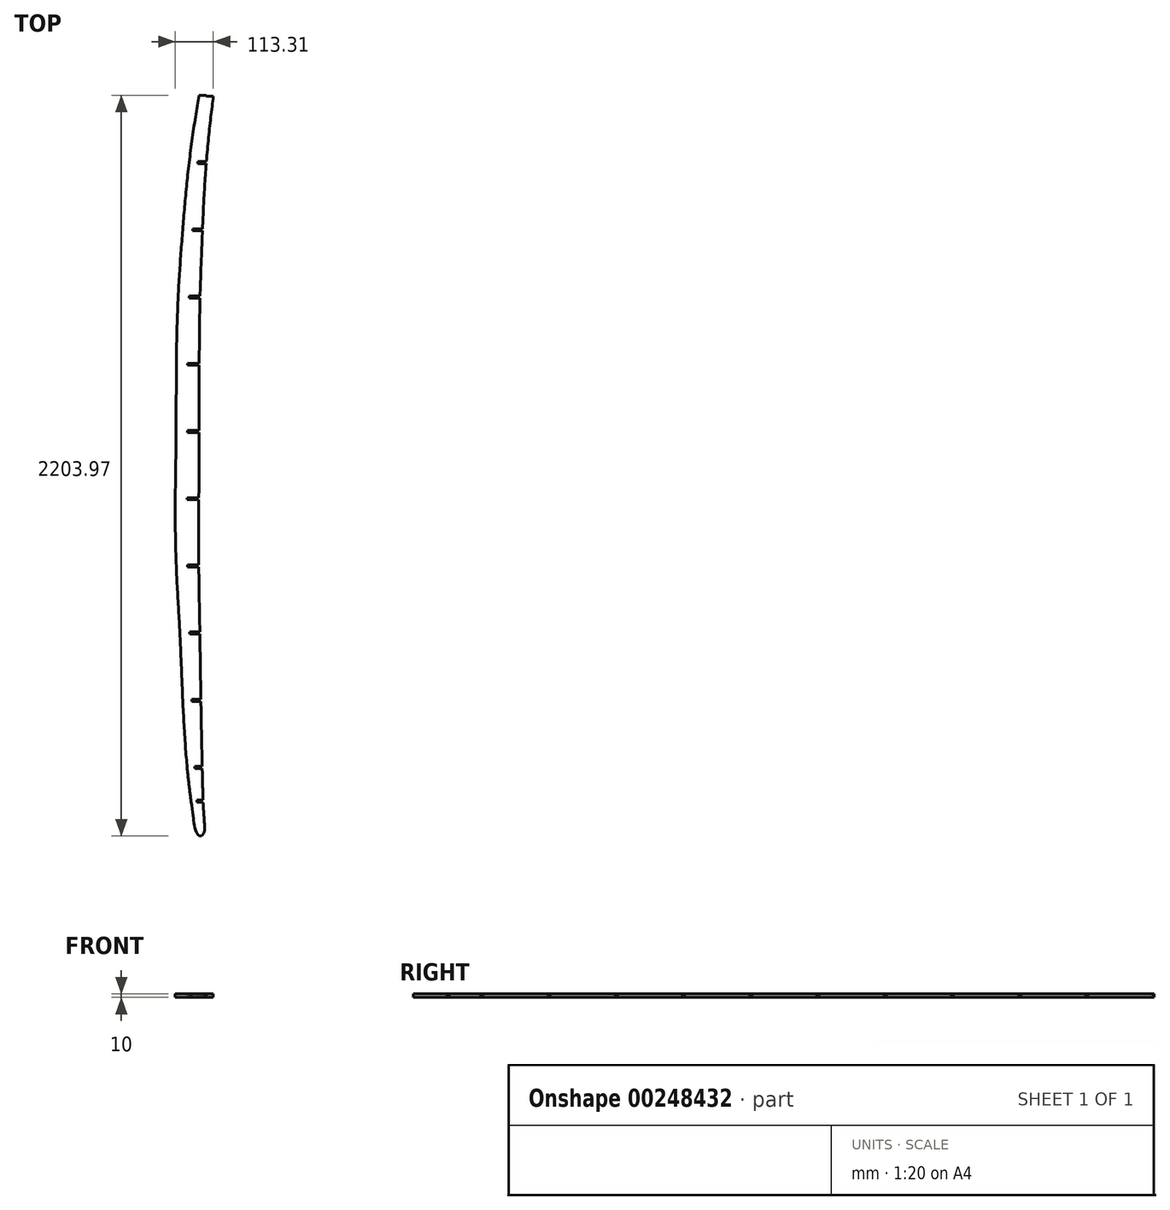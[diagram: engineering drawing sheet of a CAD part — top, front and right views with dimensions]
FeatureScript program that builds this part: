
annotation { "Feature Type Name" : "Feature", "Feature Type Description" : "" }
export const myFeature = defineFeature(function(context is Context, id is Id, definition is map)
    precondition{}
    {
        {
            var Q0;
            Q0=qCreatedBy(makeId("Top.planeOp"),FACE);
            var sketch = newSketch(context, id + "F0", { "sketchPlane" : qUnion([Q0])});
            skPoint(sketch, "E0", {"position": v(-30.92, -1091.45) * mm});
            skPoint(sketch, "E1", {"position": v(-74.7, -1091.45) * mm});
            skPoint(sketch, "E2", {"position": v(-32.04, -991.45) * mm});
            skPoint(sketch, "E3", {"position": v(-34.86, -791.45) * mm});
            skPoint(sketch, "E4", {"position": v(-87.5, -991.45) * mm});
            skPoint(sketch, "E5", {"position": v(-101.73, -791.45) * mm});
            skPoint(sketch, "E6", {"position": v(-110.44, -591.45) * mm});
            skPoint(sketch, "E7", {"position": v(-37.71, -591.45) * mm});
            skPoint(sketch, "E8", {"position": v(-40, -391.45) * mm});
            skPoint(sketch, "E9", {"position": v(-122.19, -391.45) * mm});
            skPoint(sketch, "E10", {"position": v(-125.56, -191.45) * mm});
            skPoint(sketch, "E11", {"position": v(-39.3, -191.45) * mm});
            skPoint(sketch, "E12", {"position": v(-122.68, 8.55) * mm});
            skPoint(sketch, "E13", {"position": v(-38.86, 8.55) * mm});
            skPoint(sketch, "E14", {"position": v(-38.9, 208.55) * mm});
            skPoint(sketch, "E15", {"position": v(-121.72, 208.55) * mm});
            skPoint(sketch, "E16", {"position": v(-36.32, 408.55) * mm});
            skPoint(sketch, "E17", {"position": v(-116.35, 408.55) * mm});
            skPoint(sketch, "E18", {"position": v(-29.25, 608.55) * mm});
            skPoint(sketch, "E19", {"position": v(-102.65, 608.55) * mm});
            skPoint(sketch, "E20", {"position": v(-19.1, 808.55) * mm});
            skPoint(sketch, "E21", {"position": v(-82.4, 808.55) * mm});
            skPoint(sketch, "E22", {"position": v(1.8, 1008.55) * mm});
            skPoint(sketch, "E23", {"position": v(-52.56, 1008.55) * mm});
            skPoint(sketch, "E24", {"position": v(14.1, 1108.55) * mm});
            skPoint(sketch, "E25", {"position": v(-32.64, 1108.55) * mm});
            skPoint(sketch, "E26", {"position": v(-32.6, 1108.55) * mm});
            skLineSegment(sketch, "E27", {"start": v(14.1, 1108.55) * mm, "end": v(-32.64, 1108.55) * mm});
            skLineSegment(sketch, "E28", {"start": v(1.8, 1008.55) * mm, "end": v(-52.56, 1008.55) * mm});
            skLineSegment(sketch, "E29", {"start": v(-25.38, 1008.55) * mm, "end": v(1.8, 1008.55) * mm});
            skLineSegment(sketch, "E30", {"start": v(-19.1, 808.55) * mm, "end": v(-82.4, 808.55) * mm});
            skPoint(sketch, "E31.endSnap0", {"position": v(-50.75, 808.55) * mm});
            skLineSegment(sketch, "E32", {"start": v(-29.25, 608.55) * mm, "end": v(-102.65, 608.55) * mm});
            skLineSegment(sketch, "E33", {"start": v(-36.32, 408.55) * mm, "end": v(-116.35, 408.55) * mm});
            skLineSegment(sketch, "E34", {"start": v(-38.9, 208.55) * mm, "end": v(-121.72, 208.55) * mm});
            skLineSegment(sketch, "E35", {"start": v(-38.86, 8.55) * mm, "end": v(-122.68, 8.55) * mm});
            skLineSegment(sketch, "E36", {"start": v(-39.3, -191.45) * mm, "end": v(-125.56, -191.45) * mm});
            skLineSegment(sketch, "E37", {"start": v(-40, -391.45) * mm, "end": v(-122.19, -391.45) * mm});
            skLineSegment(sketch, "E38", {"start": v(-37.71, -591.45) * mm, "end": v(-110.44, -591.45) * mm});
            skLineSegment(sketch, "E39", {"start": v(-34.86, -791.45) * mm, "end": v(-101.73, -791.45) * mm});
            skLineSegment(sketch, "E40", {"start": v(-34.86, -791.45) * mm, "end": v(-68.3, -791.45) * mm});
            skLineSegment(sketch, "E41", {"start": v(-32.04, -991.45) * mm, "end": v(-87.5, -991.45) * mm});
            skLineSegment(sketch, "E42", {"start": v(-30.92, -1091.45) * mm, "end": v(-74.7, -1091.45) * mm});
            skPoint(sketch, "E43.endSnap0", {"position": v(-52.82, -1091.45) * mm});
            skLineSegment(sketch, "E44", {"start": v(-32.64, 1108.55) * mm, "end": v(-28.25, 1108.55) * mm});
            skLineSegment(sketch, "E45", {"start": v(-28.25, 1108.55) * mm, "end": v(9.75, 1108.55) * mm});
            skLineSegment(sketch, "E46", {"start": v(9.75, 1108.55) * mm, "end": v(14.1, 1108.55) * mm});
            skLineSegment(sketch, "E47", {"start": v(14.02, 1212.5) * mm, "end": v(14.02, 1243.38) * mm});
            skLineSegment(sketch, "E48", {"start": v(27.97, 1200.3) * mm, "end": v(27.97, 1247.02) * mm});
            skFitSpline(sketch, "E49", {"points": [v(9.75, 1108.55) * mm, v(20.39, 1156.4) * mm, v(23.47, 1182.1) * mm, v(20.65, 1203.18) * mm, v(14.02, 1212.5) * mm, v(2.91, 1207.55) * mm, v(-4.03, 1195.2) * mm, v(-15.85, 1160.5) * mm, v(-28.25, 1108.55) * mm], "startDerivative": vector(69.99, 299.65) * mm, "endDerivative": vector(-63.8, -297.22) * mm});
            skLineSegment(sketch, "E50", {"start": v(-52.56, 1008.55) * mm, "end": v(-46.89, 1008.55) * mm});
            skLineSegment(sketch, "E51", {"start": v(-46.89, 1008.55) * mm, "end": v(-3.88, 1008.55) * mm});
            skLineSegment(sketch, "E52", {"start": v(-3.88, 1008.55) * mm, "end": v(1.8, 1008.55) * mm});
            skLineSegment(sketch, "E53", {"start": v(-19.1, 808.55) * mm, "end": v(-25.25, 808.55) * mm});
            skLineSegment(sketch, "E54", {"start": v(-25.25, 808.55) * mm, "end": v(-76.25, 808.55) * mm});
            skLineSegment(sketch, "E55", {"start": v(-76.25, 808.55) * mm, "end": v(-82.4, 808.55) * mm});
            skLineSegment(sketch, "E56", {"start": v(-29.25, 608.55) * mm, "end": v(-36.45, 608.55) * mm});
            skLineSegment(sketch, "E57", {"start": v(-36.45, 608.55) * mm, "end": v(-95.45, 608.55) * mm});
            skLineSegment(sketch, "E58", {"start": v(-95.45, 608.55) * mm, "end": v(-102.65, 608.55) * mm});
            skLineSegment(sketch, "E59", {"start": v(-36.32, 408.55) * mm, "end": v(-43.82, 408.55) * mm});
            skLineSegment(sketch, "E60", {"start": v(-43.82, 408.55) * mm, "end": v(-108.85, 408.55) * mm});
            skLineSegment(sketch, "E61", {"start": v(-108.85, 408.55) * mm, "end": v(-116.35, 408.55) * mm});
            skLineSegment(sketch, "E62", {"start": v(-38.9, 208.55) * mm, "end": v(-46.3, 208.55) * mm});
            skLineSegment(sketch, "E63", {"start": v(-46.3, 208.55) * mm, "end": v(-114.32, 208.55) * mm});
            skLineSegment(sketch, "E64", {"start": v(-114.32, 208.55) * mm, "end": v(-121.72, 208.55) * mm});
            skLineSegment(sketch, "E65", {"start": v(-38.86, 8.55) * mm, "end": v(-46.57, 8.55) * mm});
            skLineSegment(sketch, "E66", {"start": v(-46.57, 8.55) * mm, "end": v(-114.97, 8.55) * mm});
            skLineSegment(sketch, "E67", {"start": v(-114.97, 8.55) * mm, "end": v(-122.68, 8.55) * mm});
            skLineSegment(sketch, "E68", {"start": v(-39.3, -191.45) * mm, "end": v(-47.42, -191.45) * mm});
            skLineSegment(sketch, "E69", {"start": v(-47.42, -191.45) * mm, "end": v(-117.43, -191.45) * mm});
            skLineSegment(sketch, "E70", {"start": v(-117.43, -191.45) * mm, "end": v(-125.56, -191.45) * mm});
            skLineSegment(sketch, "E71", {"start": v(-40, -391.45) * mm, "end": v(-47.6, -391.45) * mm});
            skLineSegment(sketch, "E72", {"start": v(-47.6, -391.45) * mm, "end": v(-114.6, -391.45) * mm});
            skLineSegment(sketch, "E73", {"start": v(-114.6, -391.45) * mm, "end": v(-122.19, -391.45) * mm});
            skLineSegment(sketch, "E74", {"start": v(-37.71, -591.45) * mm, "end": v(-44.37, -591.45) * mm});
            skLineSegment(sketch, "E75", {"start": v(-44.37, -591.45) * mm, "end": v(-103.78, -591.45) * mm});
            skLineSegment(sketch, "E76", {"start": v(-103.78, -591.45) * mm, "end": v(-110.44, -591.45) * mm});
            skLineSegment(sketch, "E77", {"start": v(-34.86, -791.45) * mm, "end": v(-41.3, -791.45) * mm});
            skLineSegment(sketch, "E78", {"start": v(-41.3, -791.45) * mm, "end": v(-95.29, -791.45) * mm});
            skLineSegment(sketch, "E79", {"start": v(-95.29, -791.45) * mm, "end": v(-101.73, -791.45) * mm});
            skLineSegment(sketch, "E80", {"start": v(-32.04, -991.45) * mm, "end": v(-37.39, -991.45) * mm});
            skLineSegment(sketch, "E81", {"start": v(-37.39, -991.45) * mm, "end": v(-82.16, -991.45) * mm});
            skLineSegment(sketch, "E82", {"start": v(-82.16, -991.45) * mm, "end": v(-87.5, -991.45) * mm});
            skLineSegment(sketch, "E83", {"start": v(-30.92, -1091.45) * mm, "end": v(-35.01, -1091.45) * mm});
            skLineSegment(sketch, "E84", {"start": v(-35.01, -1091.45) * mm, "end": v(-70.62, -1091.45) * mm});
            skLineSegment(sketch, "E85", {"start": v(-70.62, -1091.45) * mm, "end": v(-74.7, -1091.45) * mm});
            skFitSpline(sketch, "E86", {"points": [v(9.75, 1108.55) * mm, v(-3.88, 1008.55) * mm, v(-25.25, 808.55) * mm, v(-36.45, 608.55) * mm, v(-43.82, 408.55) * mm, v(-46.3, 208.55) * mm, v(-46.57, 8.55) * mm, v(-47.42, -191.45) * mm, v(-47.6, -391.45) * mm, v(-44.37, -591.45) * mm, v(-41.3, -791.45) * mm, v(-37.39, -991.45) * mm, v(-35.01, -1091.45) * mm], "startDerivative": vector(-207.13, -1457.4) * mm, "endDerivative": vector(36.18, -1464.69) * mm});
            skFitSpline(sketch, "E87", {"points": [v(-35.01, -1091.45) * mm, v(-33.1, -1121.3) * mm, v(-30.99, -1153.32) * mm], "startDerivative": vector(3.84, -60.24) * mm, "endDerivative": vector(4.21, -63.47) * mm});
            skFitSpline(sketch, "E88", {"points": [v(-28.25, 1108.55) * mm, v(-46.89, 1008.55) * mm, v(-76.25, 808.55) * mm, v(-95.45, 608.55) * mm, v(-108.85, 408.55) * mm, v(-114.32, 208.55) * mm, v(-114.97, 8.55) * mm, v(-117.43, -191.45) * mm, v(-114.6, -391.45) * mm, v(-103.78, -591.45) * mm, v(-95.29, -791.45) * mm, v(-82.16, -991.45) * mm, v(-70.62, -1091.45) * mm], "startDerivative": vector(-284.6, -1452.48) * mm, "endDerivative": vector(190.25, -1460.4) * mm});
            skFitSpline(sketch, "E89", {"points": [v(-70.62, -1091.45) * mm, v(-63.97, -1136.64) * mm, v(-61.87, -1157.67) * mm, v(-56.4, -1179.96) * mm, v(-50.93, -1190.9) * mm, v(-43.78, -1195.41) * mm, v(-36.63, -1191.74) * mm, v(-31.59, -1182.06) * mm, v(-30.32, -1169.87) * mm, v(-30.99, -1153.32) * mm], "startDerivative": vector(43.58, -267.95) * mm, "endDerivative": vector(-8.77, 152.7) * mm});
            skLineSegment(sketch, "E90", {"start": v(9.75, 1108.55) * mm, "end": v(-9.25, 1108.55) * mm});
            skLineSegment(sketch, "E91", {"start": v(-9.25, 1108.55) * mm, "end": v(-9.25, 1111.55) * mm});
            skLineSegment(sketch, "E92", {"start": v(-9.25, 1108.55) * mm, "end": v(-9.25, 1105.55) * mm});
            skLineSegment(sketch, "E93", {"start": v(-9.25, 1111.55) * mm, "end": v(10.45, 1111.55) * mm});
            skLineSegment(sketch, "E94", {"start": v(-9.25, 1105.55) * mm, "end": v(9.32, 1105.55) * mm});
            skLineSegment(sketch, "E95", {"start": v(-25.38, 1008.55) * mm, "end": v(-25.38, 1011.55) * mm});
            skLineSegment(sketch, "E96", {"start": v(-25.38, 1008.55) * mm, "end": v(-25.38, 1005.55) * mm});
            skLineSegment(sketch, "E97", {"start": v(-25.38, 1011.55) * mm, "end": v(-3.5, 1011.55) * mm});
            skLineSegment(sketch, "E98", {"start": v(-25.38, 1005.55) * mm, "end": v(-4.26, 1005.55) * mm});
            skLineSegment(sketch, "E99", {"start": v(-50.75, 808.55) * mm, "end": v(-50.75, 811.55) * mm});
            skLineSegment(sketch, "E100", {"start": v(-50.75, 808.55) * mm, "end": v(-50.8, 805.55) * mm});
            skLineSegment(sketch, "E101", {"start": v(-50.75, 811.55) * mm, "end": v(-25, 811.55) * mm});
            skLineSegment(sketch, "E102", {"start": v(-50.8, 805.55) * mm, "end": v(-25.5, 805.55) * mm});
            skLineSegment(sketch, "E103", {"start": v(-65.95, 608.55) * mm, "end": v(-65.95, 611.55) * mm});
            skPoint(sketch, "E103.endSnap0", {"position": v(-65.95, 608.55) * mm});
            skLineSegment(sketch, "E104", {"start": v(-65.95, 608.55) * mm, "end": v(-65.95, 605.55) * mm});
            skLineSegment(sketch, "E105", {"start": v(-65.95, 605.55) * mm, "end": v(-36.58, 605.55) * mm});
            skLineSegment(sketch, "E106", {"start": v(-65.95, 611.55) * mm, "end": v(-36.32, 611.55) * mm});
            skLineSegment(sketch, "E107", {"start": v(-76.34, 408.55) * mm, "end": v(-76.34, 411.55) * mm});
            skLineSegment(sketch, "E108", {"start": v(-76.34, 408.55) * mm, "end": v(-76.34, 405.55) * mm});
            skLineSegment(sketch, "E109", {"start": v(-76.34, 411.55) * mm, "end": v(-43.75, 411.55) * mm});
            skLineSegment(sketch, "E110", {"start": v(-76.34, 405.55) * mm, "end": v(-43.9, 405.55) * mm});
            skLineSegment(sketch, "E111", {"start": v(-80.31, 208.55) * mm, "end": v(-80.31, 211.55) * mm});
            skLineSegment(sketch, "E112", {"start": v(-80.31, 208.55) * mm, "end": v(-80.31, 205.55) * mm});
            skLineSegment(sketch, "E113", {"start": v(-80.31, 211.55) * mm, "end": v(-46.29, 211.55) * mm});
            skLineSegment(sketch, "E114", {"start": v(-80.31, 205.55) * mm, "end": v(-46.3, 205.55) * mm});
            skLineSegment(sketch, "E115", {"start": v(-80.77, 8.55) * mm, "end": v(-80.77, 11.55) * mm});
            skLineSegment(sketch, "E116", {"start": v(-80.77, 8.55) * mm, "end": v(-80.77, 5.55) * mm});
            skLineSegment(sketch, "E117", {"start": v(-80.77, 11.55) * mm, "end": v(-46.57, 11.55) * mm});
            skLineSegment(sketch, "E118", {"start": v(-80.77, 5.55) * mm, "end": v(-46.58, 5.55) * mm});
            skLineSegment(sketch, "E119", {"start": v(-82.43, -191.45) * mm, "end": v(-82.43, -188.45) * mm});
            skPoint(sketch, "E119.endSnap0", {"position": v(-82.43, -191.45) * mm});
            skLineSegment(sketch, "E120", {"start": v(-82.43, -191.45) * mm, "end": v(-82.43, -194.45) * mm});
            skLineSegment(sketch, "E121", {"start": v(-81.1, -391.45) * mm, "end": v(-81.1, -388.45) * mm});
            skLineSegment(sketch, "E122", {"start": v(-81.1, -391.45) * mm, "end": v(-81.1, -394.45) * mm});
            skLineSegment(sketch, "E123", {"start": v(-82.43, -194.45) * mm, "end": v(-47.44, -194.45) * mm});
            skLineSegment(sketch, "E124", {"start": v(-82.43, -188.45) * mm, "end": v(-47.4, -188.45) * mm});
            skLineSegment(sketch, "E125", {"start": v(-81.1, -388.45) * mm, "end": v(-47.62, -388.45) * mm});
            skLineSegment(sketch, "E126", {"start": v(-81.1, -394.45) * mm, "end": v(-47.57, -394.45) * mm});
            skLineSegment(sketch, "E127", {"start": v(-74.08, -591.45) * mm, "end": v(-74.08, -588.45) * mm});
            skPoint(sketch, "E127.endSnap0", {"position": v(-74.08, -591.45) * mm});
            skLineSegment(sketch, "E128", {"start": v(-74.08, -591.45) * mm, "end": v(-74.08, -594.45) * mm});
            skLineSegment(sketch, "E129", {"start": v(-68.3, -791.45) * mm, "end": v(-68.3, -788.45) * mm});
            skLineSegment(sketch, "E130", {"start": v(-68.3, -791.45) * mm, "end": v(-68.3, -794.45) * mm});
            skLineSegment(sketch, "E131", {"start": v(-74.08, -594.45) * mm, "end": v(-44.32, -594.45) * mm});
            skLineSegment(sketch, "E132", {"start": v(-74.08, -588.45) * mm, "end": v(-44.43, -588.45) * mm});
            skLineSegment(sketch, "E133", {"start": v(-68.3, -788.45) * mm, "end": v(-41.35, -788.45) * mm});
            skLineSegment(sketch, "E134", {"start": v(-68.3, -794.45) * mm, "end": v(-41.25, -794.45) * mm});
            skLineSegment(sketch, "E135", {"start": v(-59.78, -991.45) * mm, "end": v(-59.78, -994.45) * mm});
            skLineSegment(sketch, "E136", {"start": v(-59.78, -991.45) * mm, "end": v(-59.78, -988.45) * mm});
            skLineSegment(sketch, "E137", {"start": v(-52.82, -1091.45) * mm, "end": v(-52.82, -1088.45) * mm});
            skLineSegment(sketch, "E138", {"start": v(-52.82, -1091.45) * mm, "end": v(-52.82, -1094.45) * mm});
            skLineSegment(sketch, "E139", {"start": v(-59.78, -994.45) * mm, "end": v(-37.32, -994.45) * mm});
            skLineSegment(sketch, "E140", {"start": v(-59.78, -988.45) * mm, "end": v(-37.46, -988.45) * mm});
            skLineSegment(sketch, "E141", {"start": v(-52.82, -1088.45) * mm, "end": v(-35.09, -1088.45) * mm});
            skLineSegment(sketch, "E142", {"start": v(-52.82, -1094.45) * mm, "end": v(-34.82, -1094.45) * mm});
            skSolve(sketch);
        }
        {
            var Q0;
            {var subQ0=sQuery(id+"F0.wireOp",EDGE,"96803848-1639-48f9-b089-5a12bcde23c2");var subQ1=sQuery(id+"F0.wireOp",EDGE,"5e1cb565-0f39-446d-889c-04de5665a436");var subQ2=makeQuery(id+"F0.imprint","INTERSECT",VERTEX,{"derivedFrom":[subQ1,subQ0]});Q0=makeQuery(id+"F0.imprint","IMPRINT",FACE,{"disambiguationData":[TD([[makeQuery(id+"F0.imprint","IMPRINT",EDGE,{"disambiguationData":[TD([[subQ2,-1.0]])],"derivedFrom":subQ1}),1.0]])]});}
            var Q1;
            {var subQ0=sQuery(id+"F0.wireOp",EDGE,"9d2d0d3a-5e80-47e2-bbc4-b40661b40abf");Q1=makeQuery(id+"F0.imprint","IMPRINT",FACE,{"disambiguationData":[TD([[makeQuery(id+"F0.imprint","IMPRINT",EDGE,{"derivedFrom":subQ0}),1.0]])]});}
            var Q2;
            {var subQ3=sQuery(id+"F0.wireOp",EDGE,"191cd121-5488-4c6e-b41c-89e0bf0fb3e3");var subQ5=sQuery(id+"F0.wireOp",EDGE,"5e1cb565-0f39-446d-889c-04de5665a436");var subQ6=makeQuery(id+"F0.imprint","INTERSECT",VERTEX,{"derivedFrom":[subQ5,subQ3]});Q2=makeQuery(id+"F0.imprint","IMPRINT",FACE,{"disambiguationData":[TD([[makeQuery(id+"F0.imprint","IMPRINT",EDGE,{"disambiguationData":[TD([[subQ6,1.0]])],"derivedFrom":subQ5}),1.0]])]});}
            var Q3;
            {var subQ0=sQuery(id+"F0.wireOp",EDGE,"fca3878f-9e9c-4a64-95c8-6b51368d669e");var subQ1=sQuery(id+"F0.wireOp",EDGE,"96803848-1639-48f9-b089-5a12bcde23c2");var subQ2=makeQuery(id+"F0.imprint","INTERSECT",VERTEX,{"derivedFrom":[subQ1,subQ0]});Q3=makeQuery(id+"F0.imprint","IMPRINT",FACE,{"disambiguationData":[TD([[makeQuery(id+"F0.imprint","IMPRINT",EDGE,{"disambiguationData":[TD([[subQ2,1.0]])],"derivedFrom":subQ1}),-1.0]])]});}
            var Q4;
            {var subQ0=sQuery(id+"F0.wireOp",EDGE,"VQ11bQa7-b9hK-Ufeh-kjPI-M5ydZVCvJp6h");var subQ1=sQuery(id+"F0.wireOp",EDGE,"191cd121-5488-4c6e-b41c-89e0bf0fb3e3");var subQ2=makeQuery(id+"F0.imprint","INTERSECT",VERTEX,{"derivedFrom":[subQ1,subQ0]});Q4=makeQuery(id+"F0.imprint","IMPRINT",FACE,{"disambiguationData":[TD([[makeQuery(id+"F0.imprint","IMPRINT",EDGE,{"disambiguationData":[TD([[subQ2,-1.0]])],"derivedFrom":subQ1}),1.0]])]});}
            var Q5;
            {var subQ0=sQuery(id+"F0.wireOp",EDGE,"rgXr4bSv-tqgH-3edv-LkYs-uhf3zUF2Z0sS");var subQ1=sQuery(id+"F0.wireOp",EDGE,"191cd121-5488-4c6e-b41c-89e0bf0fb3e3");var subQ2=makeQuery(id+"F0.imprint","INTERSECT",VERTEX,{"derivedFrom":[subQ1,subQ0]});Q5=makeQuery(id+"F0.imprint","IMPRINT",FACE,{"disambiguationData":[TD([[makeQuery(id+"F0.imprint","IMPRINT",EDGE,{"disambiguationData":[TD([[subQ2,-1.0]])],"derivedFrom":subQ1}),1.0]])]});}
            var Q6;
            {var subQ0=sQuery(id+"F0.wireOp",EDGE,"HgmTktwH-ycFn-5ByA-DDyz-7d7K9y9TTn39");var subQ1=sQuery(id+"F0.wireOp",EDGE,"191cd121-5488-4c6e-b41c-89e0bf0fb3e3");var subQ2=makeQuery(id+"F0.imprint","INTERSECT",VERTEX,{"derivedFrom":[subQ1,subQ0]});Q6=makeQuery(id+"F0.imprint","IMPRINT",FACE,{"disambiguationData":[TD([[makeQuery(id+"F0.imprint","IMPRINT",EDGE,{"disambiguationData":[TD([[subQ2,-1.0]])],"derivedFrom":subQ1}),1.0]])]});}
            var Q7;
            {var subQ0=sQuery(id+"F0.wireOp",EDGE,"sFE5uWUb-kEtP-6kAt-UajO-OYiFYuNbIUM7");var subQ1=sQuery(id+"F0.wireOp",EDGE,"191cd121-5488-4c6e-b41c-89e0bf0fb3e3");var subQ2=makeQuery(id+"F0.imprint","INTERSECT",VERTEX,{"derivedFrom":[subQ1,subQ0]});Q7=makeQuery(id+"F0.imprint","IMPRINT",FACE,{"disambiguationData":[TD([[makeQuery(id+"F0.imprint","IMPRINT",EDGE,{"disambiguationData":[TD([[subQ2,-1.0]])],"derivedFrom":subQ1}),1.0]])]});}
            var Q8;
            {var subQ0=sQuery(id+"F0.wireOp",EDGE,"3OWxYksK-VBRC-Qdfa-MlbK-5JrUo6AgJBi3");var subQ1=sQuery(id+"F0.wireOp",EDGE,"191cd121-5488-4c6e-b41c-89e0bf0fb3e3");var subQ2=makeQuery(id+"F0.imprint","INTERSECT",VERTEX,{"derivedFrom":[subQ1,subQ0]});Q8=makeQuery(id+"F0.imprint","IMPRINT",FACE,{"disambiguationData":[TD([[makeQuery(id+"F0.imprint","IMPRINT",EDGE,{"disambiguationData":[TD([[subQ2,-1.0]])],"derivedFrom":subQ1}),1.0]])]});}
            var Q9;
            {var subQ7=sQuery(id+"F0.wireOp",EDGE,"b95d8d61-5619-4274-85c0-0d5589efb3a8");var subQ9=sQuery(id+"F0.wireOp",EDGE,"191cd121-5488-4c6e-b41c-89e0bf0fb3e3");var subQ10=makeQuery(id+"F0.imprint","INTERSECT",VERTEX,{"derivedFrom":[subQ9,subQ7]});Q9=makeQuery(id+"F0.imprint","IMPRINT",FACE,{"disambiguationData":[TD([[makeQuery(id+"F0.imprint","IMPRINT",EDGE,{"disambiguationData":[TD([[subQ10,1.0]])],"derivedFrom":subQ9}),1.0]])]});}
            var Q10;
            {var subQ0=sQuery(id+"F0.wireOp",EDGE,"WZ9AN37Y-7knb-OkOB-LRKc-X5aR3kHhT85A");var subQ1=sQuery(id+"F0.wireOp",EDGE,"b95d8d61-5619-4274-85c0-0d5589efb3a8");var subQ2=makeQuery(id+"F0.imprint","INTERSECT",VERTEX,{"derivedFrom":[subQ1,subQ0]});Q10=makeQuery(id+"F0.imprint","IMPRINT",FACE,{"disambiguationData":[TD([[makeQuery(id+"F0.imprint","IMPRINT",EDGE,{"disambiguationData":[TD([[subQ2,-1.0]])],"derivedFrom":subQ1}),1.0]])]});}
            var Q11;
            {var subQ0=sQuery(id+"F0.wireOp",EDGE,"H0WRzIU7-0eJz-28J9-xl7T-ptnePE7jlNnf");var subQ1=sQuery(id+"F0.wireOp",EDGE,"b95d8d61-5619-4274-85c0-0d5589efb3a8");var subQ2=makeQuery(id+"F0.imprint","INTERSECT",VERTEX,{"derivedFrom":[subQ1,subQ0]});Q11=makeQuery(id+"F0.imprint","IMPRINT",FACE,{"disambiguationData":[TD([[makeQuery(id+"F0.imprint","IMPRINT",EDGE,{"disambiguationData":[TD([[subQ2,-1.0]])],"derivedFrom":subQ1}),1.0]])]});}
            var Q12;
            {var subQ0=sQuery(id+"F0.wireOp",EDGE,"iVFNM8Ld-HWw0-vMhU-tXVe-9rH3Qs5w4x78");var subQ1=sQuery(id+"F0.wireOp",EDGE,"b95d8d61-5619-4274-85c0-0d5589efb3a8");var subQ2=makeQuery(id+"F0.imprint","INTERSECT",VERTEX,{"derivedFrom":[subQ1,subQ0]});Q12=makeQuery(id+"F0.imprint","IMPRINT",FACE,{"disambiguationData":[TD([[makeQuery(id+"F0.imprint","IMPRINT",EDGE,{"disambiguationData":[TD([[subQ2,-1.0]])],"derivedFrom":subQ1}),1.0]])]});}
            var Q13;
            {var subQ0=sQuery(id+"F0.wireOp",EDGE,"cJeIJZ6n-enJI-ftBn-iPWl-IRGfeO3FElIz");var subQ1=sQuery(id+"F0.wireOp",EDGE,"b95d8d61-5619-4274-85c0-0d5589efb3a8");var subQ2=makeQuery(id+"F0.imprint","INTERSECT",VERTEX,{"derivedFrom":[subQ1,subQ0]});Q13=makeQuery(id+"F0.imprint","IMPRINT",FACE,{"disambiguationData":[TD([[makeQuery(id+"F0.imprint","IMPRINT",EDGE,{"disambiguationData":[TD([[subQ2,1.0]])],"derivedFrom":subQ1}),1.0]])]});}
            var Q14;
            {var subQ5=sQuery(id+"F0.wireOp",EDGE,"E45");Q14=makeQuery(id+"F0.imprint","IMPRINT",FACE,{"disambiguationData":[TD([[makeQuery(id+"F0.imprint","IMPRINT",EDGE,{"derivedFrom":subQ5}),-1.0]])]});}
            var Q15;
            {var subQ0=sQuery(id+"F0.wireOp",EDGE,"E45");Q15=makeQuery(id+"F0.imprint","IMPRINT",FACE,{"disambiguationData":[TD([[makeQuery(id+"F0.imprint","IMPRINT",EDGE,{"derivedFrom":subQ0}),1.0]])]});}
            var Q16;
            {var subQ8=sQuery(id+"F0.wireOp",EDGE,"E96");Q16=makeQuery(id+"F0.imprint","IMPRINT",FACE,{"disambiguationData":[TD([[makeQuery(id+"F0.imprint","IMPRINT",EDGE,{"derivedFrom":subQ8}),-1.0]])]});}
            var Q17;
            {var subQ9=sQuery(id+"F0.wireOp",EDGE,"E100");Q17=makeQuery(id+"F0.imprint","IMPRINT",FACE,{"disambiguationData":[TD([[makeQuery(id+"F0.imprint","IMPRINT",EDGE,{"derivedFrom":subQ9}),-1.0]])]});}
            var Q18;
            {var subQ9=sQuery(id+"F0.wireOp",EDGE,"E104");Q18=makeQuery(id+"F0.imprint","IMPRINT",FACE,{"disambiguationData":[TD([[makeQuery(id+"F0.imprint","IMPRINT",EDGE,{"derivedFrom":subQ9}),-1.0]])]});}
            var Q19;
            {var subQ9=sQuery(id+"F0.wireOp",EDGE,"E108");Q19=makeQuery(id+"F0.imprint","IMPRINT",FACE,{"disambiguationData":[TD([[makeQuery(id+"F0.imprint","IMPRINT",EDGE,{"derivedFrom":subQ9}),-1.0]])]});}
            var Q20;
            {var subQ5=sQuery(id+"F0.wireOp",EDGE,"E112");Q20=makeQuery(id+"F0.imprint","IMPRINT",FACE,{"disambiguationData":[TD([[makeQuery(id+"F0.imprint","IMPRINT",EDGE,{"derivedFrom":subQ5}),-1.0]])]});}
            var Q21;
            {var subQ5=sQuery(id+"F0.wireOp",EDGE,"E135");Q21=makeQuery(id+"F0.imprint","IMPRINT",FACE,{"disambiguationData":[TD([[makeQuery(id+"F0.imprint","IMPRINT",EDGE,{"derivedFrom":subQ5}),-1.0]])]});}
            var Q22;
            {var subQ0=sQuery(id+"F0.wireOp",EDGE,"E89");Q22=makeQuery(id+"F0.imprint","IMPRINT",FACE,{"disambiguationData":[TD([[makeQuery(id+"F0.imprint","IMPRINT",EDGE,{"derivedFrom":subQ0}),1.0]])]});}
            var Q23;
            {var subQ5=sQuery(id+"F0.wireOp",EDGE,"E130");Q23=makeQuery(id+"F0.imprint","IMPRINT",FACE,{"disambiguationData":[TD([[makeQuery(id+"F0.imprint","IMPRINT",EDGE,{"derivedFrom":subQ5}),-1.0]])]});}
            var Q24;
            {var subQ9=sQuery(id+"F0.wireOp",EDGE,"E128");Q24=makeQuery(id+"F0.imprint","IMPRINT",FACE,{"disambiguationData":[TD([[makeQuery(id+"F0.imprint","IMPRINT",EDGE,{"derivedFrom":subQ9}),-1.0]])]});}
            var Q25;
            {var subQ9=sQuery(id+"F0.wireOp",EDGE,"E122");Q25=makeQuery(id+"F0.imprint","IMPRINT",FACE,{"disambiguationData":[TD([[makeQuery(id+"F0.imprint","IMPRINT",EDGE,{"derivedFrom":subQ9}),-1.0]])]});}
            var Q26;
            {var subQ9=sQuery(id+"F0.wireOp",EDGE,"E116");Q26=makeQuery(id+"F0.imprint","IMPRINT",FACE,{"disambiguationData":[TD([[makeQuery(id+"F0.imprint","IMPRINT",EDGE,{"derivedFrom":subQ9}),-1.0]])]});}
            var Q27;
            {var subQ5=sQuery(id+"F0.wireOp",EDGE,"E120");Q27=makeQuery(id+"F0.imprint","IMPRINT",FACE,{"disambiguationData":[TD([[makeQuery(id+"F0.imprint","IMPRINT",EDGE,{"derivedFrom":subQ5}),-1.0]])]});}
            extrude(context, id + "F1", {"entities" : qUnion([Q0, Q1, Q2, Q3, Q4, Q5, Q6, Q7, Q8, Q9, Q10, Q11, Q12, Q13, Q14, Q15, Q16, Q17, Q18, Q19, Q20, Q21, Q22, Q23, Q24, Q25, Q26, Q27]), "depth" : 10 * mm});
        }
    });
